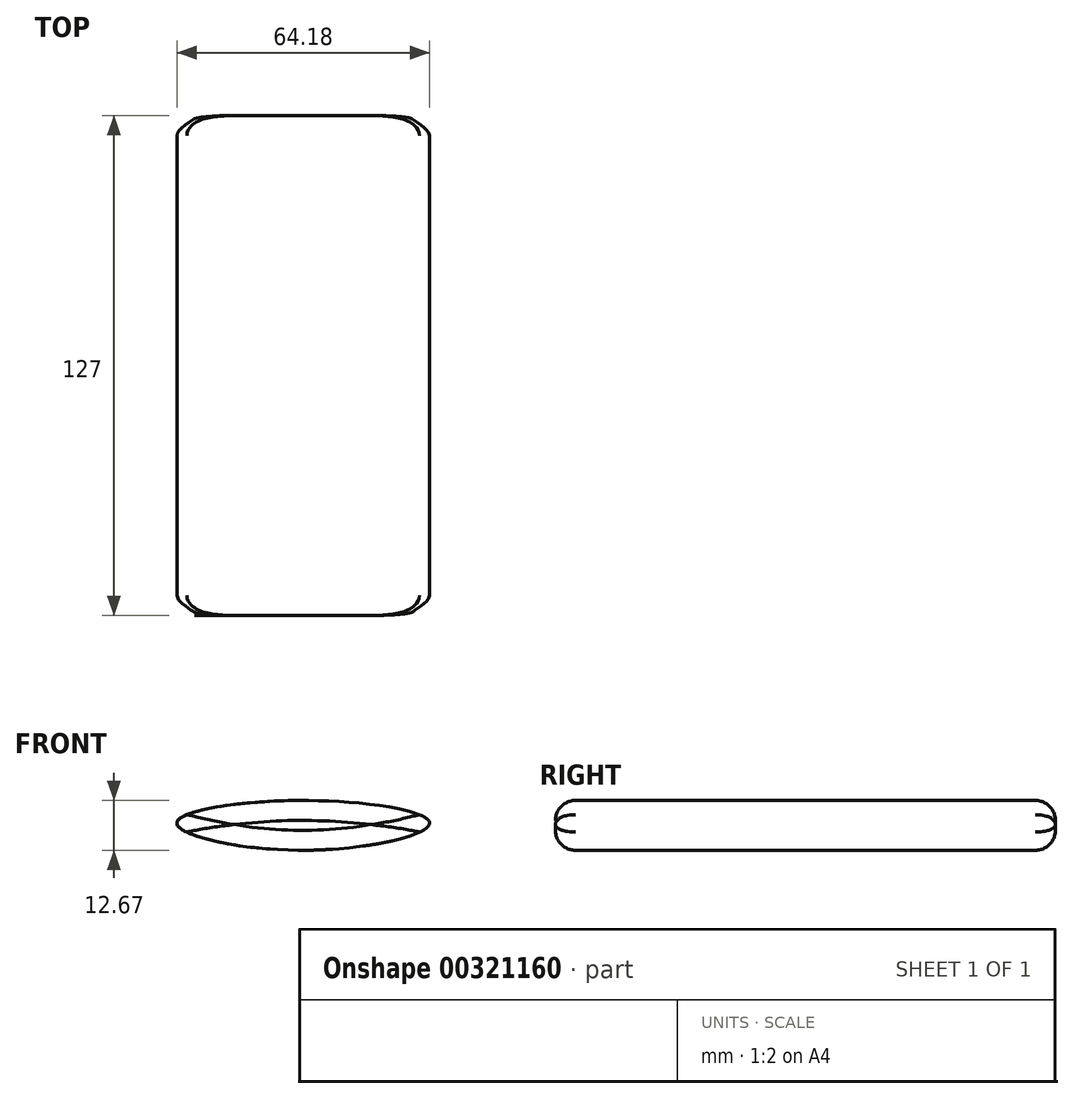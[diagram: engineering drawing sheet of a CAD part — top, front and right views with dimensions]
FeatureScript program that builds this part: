
annotation { "Feature Type Name" : "Feature", "Feature Type Description" : "" }
export const myFeature = defineFeature(function(context is Context, id is Id, definition is map)
    precondition{}
    {
        {
            var Q0;
            Q0=qCreatedBy(makeId("Front.planeOp"),FACE);
            var sketch = newSketch(context, id + "F0", { "sketchPlane" : qUnion([Q0])});
            skFitSpline(sketch, "E0", {"points": [v(-31.66, 0) * mm, v(0, 5.76) * mm, v(32.52, 0) * mm, v(0, -6.9) * mm, v(-31.66, 0) * mm]});
            skSolve(sketch);
        }
        {
            var Q0;
            Q0 = qSketchRegion(id + "F0", true);
            extrude(context, id + "F1", {"entities" : qUnion([Q0]), "depth" : 127 * mm});
        }
        {
            var Q0;
            Q0=makeQuery(id+"F1.opExtrude","CAP_EDGE",EDGE,{"disambiguationData":[OSD([sQuery(id+"F0.wireOp",EDGE,"E0")])],"isStart":false});
            var Q1;
            Q1=makeQuery(id+"F1.opExtrude","CAP_EDGE",EDGE,{"disambiguationData":[OSD([sQuery(id+"F0.wireOp",EDGE,"E0")])],"isStart":true});
            fillet(context, id + "F2", {"entities" : qUnion([Q0, Q1]), "radius" : 5.08 * mm, "tangentPropagation" : true, "allowEdgeOverflow" : false});
        }
    });
